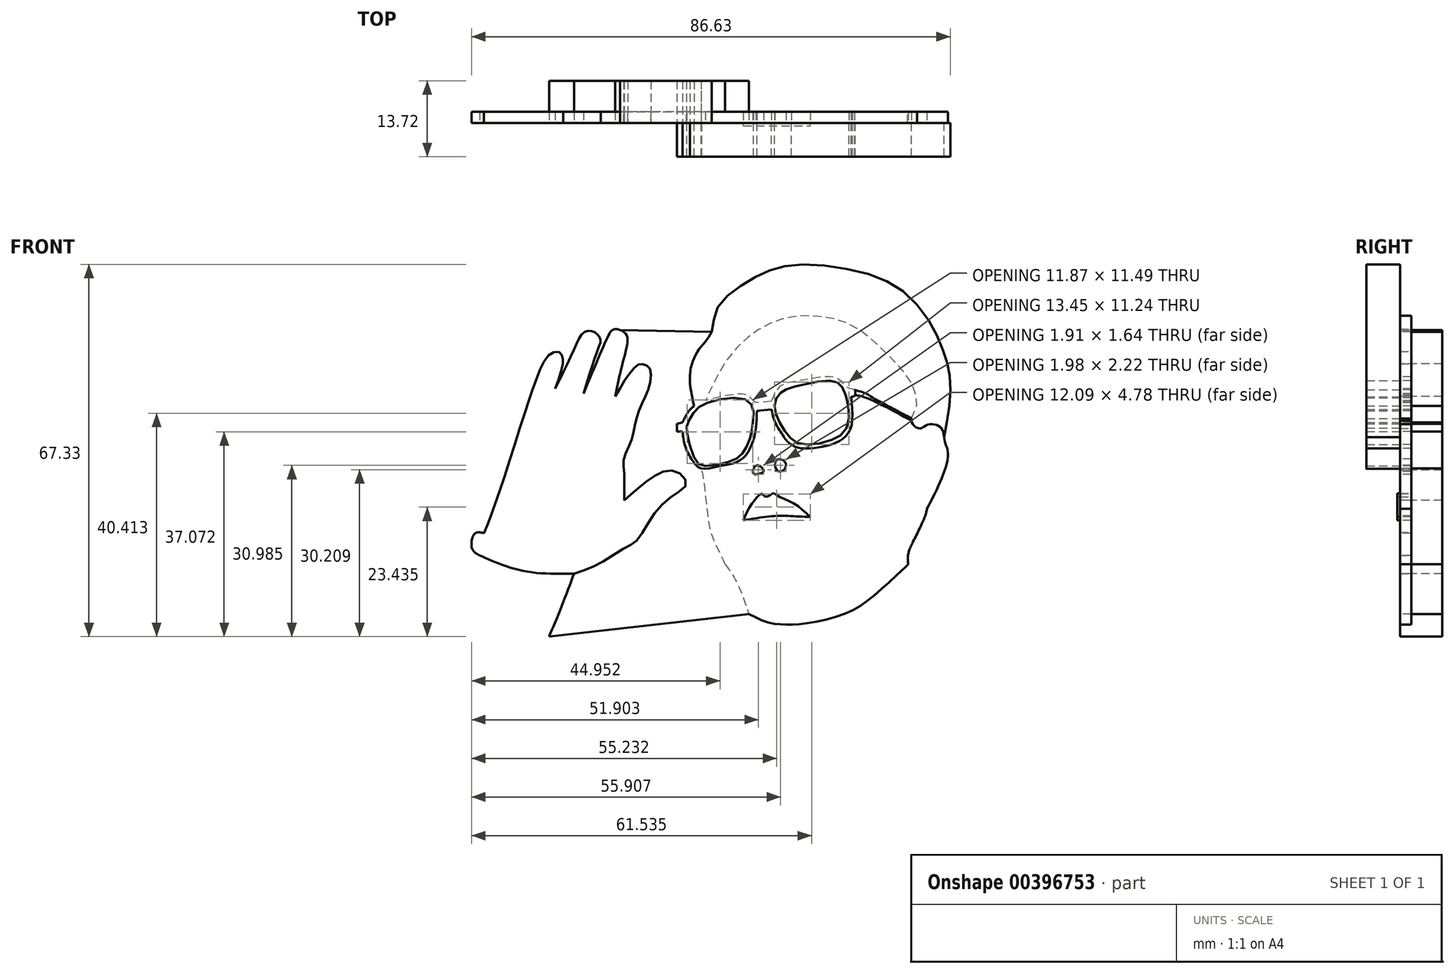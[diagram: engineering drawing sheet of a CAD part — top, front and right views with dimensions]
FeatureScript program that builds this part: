
annotation { "Feature Type Name" : "Feature", "Feature Type Description" : "" }
export const myFeature = defineFeature(function(context is Context, id is Id, definition is map)
    precondition{}
    {
        {
            var Q0;
            Q0=qCreatedBy(makeId("Front.planeOp"),FACE);
            var sketch = newSketch(context, id + "F0", { "sketchPlane" : qUnion([Q0])});
            skFitSpline(sketch, "E0", {"points": [v(-10.9, 0) * mm, v(-12.43, 3.33) * mm, v(-13.41, 5.64) * mm, v(-14.1, 9.87) * mm, v(-15.17, 17.33) * mm, v(-15.24, 17.33) * mm], "startDerivative": vector(-7.08, 15.66) * mm, "endDerivative": vector(-2.12, -1.22) * mm});
            skFitSpline(sketch, "E1", {"points": [v(-5.76, 16.4) * mm, v(-4.7, 16.4) * mm, v(-3.91, 16.94) * mm, v(-4.74, 17.86) * mm, v(-5.18, 17.9) * mm, v(-5.71, 17.47) * mm, v(-5.76, 16.4) * mm]});
            skFitSpline(sketch, "E2", {"points": [v(-1.54, 16.98) * mm, v(-0.66, 16.84) * mm, v(0, 17.52) * mm, v(0, 18.44) * mm, v(-1.05, 19.02) * mm, v(-1.78, 18.73) * mm, v(-1.54, 16.98) * mm]});
            skFitSpline(sketch, "E3", {"points": [v(-7.6, 7.95) * mm, v(-6.4, 10.53) * mm, v(-4.93, 12.32) * mm, v(-4.2, 12.76) * mm, v(-3.72, 12.27) * mm, v(-2.85, 12.47) * mm, v(-2.26, 12.86) * mm, v(-1.24, 12.32) * mm, v(1.67, 10.91) * mm, v(4.49, 8.56) * mm], "startDerivative": vector(7.43, 18.33) * mm, "endDerivative": vector(15.87, -15.6) * mm});
            skFitSpline(sketch, "E4", {"points": [v(-7.6, 7.95) * mm, v(-3.82, 8.56) * mm, v(-0.98, 8.77) * mm, v(1.7, 8.7) * mm, v(4.49, 8.56) * mm], "startDerivative": vector(13.93, 2.45) * mm, "endDerivative": vector(11.63, -0.59) * mm});
            skFitSpline(sketch, "E5", {"points": [v(-7.6, 7.95) * mm, v(-5.68, 9.87) * mm, v(-4.23, 9.87) * mm, v(-1.91, 10.5) * mm, v(1.29, 9.87) * mm, v(4.49, 8.56) * mm], "startDerivative": vector(9.45, 12.57) * mm, "endDerivative": vector(13.65, -5.86) * mm});
            skFitSpline(sketch, "E6", {"points": [v(0.58, 16.24) * mm, v(2.34, 17.42) * mm, v(2.4, 20.12) * mm, v(1.29, 21.11) * mm, v(1.11, 21.64) * mm], "startDerivative": vector(7.2, 2.7) * mm, "endDerivative": vector(-0.35, 3.73) * mm});
            skFitSpline(sketch, "E7", {"points": [v(-5.7, 15.07) * mm, v(-7.05, 16.18) * mm, v(-7.22, 18.18) * mm, v(-5.82, 19.82) * mm], "startDerivative": vector(-4.98, 2.85) * mm, "endDerivative": vector(5, 4.2) * mm});
            skFitSpline(sketch, "E8", {"points": [v(-10.9, 0) * mm, v(-8.85, -3.14) * mm, v(-6.61, -8.97) * mm], "startDerivative": vector(4.87, -6.5) * mm, "endDerivative": vector(3.76, -11.24) * mm});
            skFitSpline(sketch, "E9", {"points": [v(-6.61, -8.97) * mm, v(-2.94, -10.56) * mm, v(0, -10.88) * mm, v(3.45, -10.72) * mm, v(10.71, -8.97) * mm, v(15.74, -5.85) * mm, v(20.85, -1.3) * mm, v(22.22, 0) * mm], "startDerivative": vector(27.5, -14.14) * mm, "endDerivative": vector(11.85, 11.52) * mm});
            skFitSpline(sketch, "E10", {"points": [v(22.22, 0) * mm, v(22.22, 1.86) * mm, v(23.68, 5.27) * mm, v(25.22, 8.6) * mm, v(25.62, 10.05) * mm], "startDerivative": vector(-1.02, 8.24) * mm, "endDerivative": vector(1.53, 6.93) * mm});
            skFitSpline(sketch, "E11", {"points": [v(23.07, 4.07) * mm, v(22.95, 5.27) * mm, v(23.68, 9.65) * mm], "startDerivative": vector(-0.65, 2.97) * mm, "endDerivative": vector(1.6, 7.7) * mm});
            skFitSpline(sketch, "E12", {"points": [v(25.62, 10.05) * mm, v(27.81, 14.51) * mm, v(29.44, 19.95) * mm, v(28.87, 22.14) * mm, v(28.54, 23.92) * mm, v(27.73, 25.06) * mm, v(25.62, 25.22) * mm, v(24.32, 24.57) * mm, v(22.95, 25.55) * mm, v(22.95, 26.93) * mm, v(23.68, 28.3) * mm, v(22.95, 32.52) * mm, v(18.08, 38.36) * mm, v(11.91, 43.31) * mm, v(4.86, 44.93) * mm, v(0, 44.53) * mm, v(-5.2, 42.26) * mm, v(-10.56, 36.98) * mm, v(-14.45, 29.6) * mm], "startDerivative": vector(34.38, 66.1) * mm, "endDerivative": vector(-42.74, -94.88) * mm});
            skFitSpline(sketch, "E13", {"points": [v(28.7, 23.02) * mm, v(29.66, 28.67) * mm, v(29.74, 33.99) * mm, v(28.87, 37.67) * mm, v(26.63, 42.99) * mm, v(21.23, 49.45) * mm, v(12.96, 53.05) * mm, v(2, 54.2) * mm, v(-3.9, 52.73) * mm, v(-9.27, 49.54) * mm, v(-12.68, 45.63) * mm, v(-13.35, 42.05) * mm, v(-15.5, 39.05) * mm, v(-17.26, 34.47) * mm, v(-16.5, 28.64) * mm], "startDerivative": vector(15.76, 79.49) * mm, "endDerivative": vector(19.32, -83.28) * mm});
            skFitSpline(sketch, "E14", {"points": [v(1.36, 26.58) * mm, v(4.9, 26.99) * mm, v(8.36, 27.56) * mm, v(5.48, 28.22) * mm, v(4.08, 28.47) * mm, v(1.36, 26.58) * mm]});
            skFitSpline(sketch, "E15", {"points": [v(3.3, 28.12) * mm, v(3.32, 27.5) * mm, v(3.66, 26.76) * mm], "startDerivative": vector(-0.1, -1.32) * mm, "endDerivative": vector(0.8, -1.48) * mm});
            skFitSpline(sketch, "E16", {"points": [v(5.48, 28.22) * mm, v(5.48, 27.64) * mm, v(5.2, 27.04) * mm], "startDerivative": vector(0.12, -1.23) * mm, "endDerivative": vector(-0.62, -1.28) * mm});
            skFitSpline(sketch, "E17", {"points": [v(-11.5, 23.7) * mm, v(-10.57, 24.74) * mm, v(-10.06, 25.18) * mm, v(-9.09, 25.38) * mm, v(-7.27, 25.28) * mm, v(-6.77, 24.88) * mm, v(-6.8, 24.85) * mm], "startDerivative": vector(4.66, 5.17) * mm, "endDerivative": vector(-1.21, -0.56) * mm});
            skFitSpline(sketch, "E18", {"points": [v(-11.5, 23.7) * mm, v(-9.7, 23.7) * mm, v(-6.77, 24.88) * mm], "startDerivative": vector(4, -0.45) * mm, "endDerivative": vector(5.41, 2.66) * mm});
            skFitSpline(sketch, "E19", {"points": [v(-10.57, 24.74) * mm, v(-10.3, 24.14) * mm, v(-9.7, 23.7) * mm], "startDerivative": vector(0.4, -1.34) * mm, "endDerivative": vector(1.34, -0.75) * mm});
            skFitSpline(sketch, "E20", {"points": [v(-8.14, 25.43) * mm, v(-8.18, 24.88) * mm, v(-8.3, 24.16) * mm], "startDerivative": vector(-0.04, -1.14) * mm, "endDerivative": vector(-0.27, -1.36) * mm});
            skFitSpline(sketch, "E21", {"points": [v(-5.15, 27.77) * mm, v(-2.53, 28) * mm], "startDerivative": vector(2.63, 0.24) * mm, "endDerivative": vector(2.63, 0.24) * mm});
            skFitSpline(sketch, "E22", {"points": [v(-2.53, 28) * mm, v(-1.8, 25.52) * mm, v(-0.7, 23.7) * mm, v(0.33, 22.25) * mm, v(1.11, 21.64) * mm], "startDerivative": vector(2.04, -8.75) * mm, "endDerivative": vector(4.25, -2.72) * mm});
            skFitSpline(sketch, "E23", {"points": [v(1.11, 21.64) * mm, v(2.22, 21.1) * mm, v(5.48, 21.07) * mm, v(9.27, 22.07) * mm, v(11.72, 24.38) * mm, v(11.89, 30.28) * mm], "startDerivative": vector(7.71, -5.2) * mm, "endDerivative": vector(-2.5, 25.05) * mm});
            skFitSpline(sketch, "E24", {"points": [v(11.89, 30.28) * mm, v(12.54, 30.57) * mm, v(12.51, 31.6) * mm, v(11.52, 31.82) * mm, v(9.67, 33.47) * mm, v(6.2, 33.84) * mm, v(2.25, 33.15) * mm, v(-0.93, 32.24) * mm, v(-2.53, 29.46) * mm], "startDerivative": vector(10.84, 1.27) * mm, "endDerivative": vector(-8.07, -21.78) * mm});
            skFitSpline(sketch, "E25", {"points": [v(-2.53, 29.46) * mm, v(-5.35, 29.22) * mm], "startDerivative": vector(-2.82, -0.24) * mm, "endDerivative": vector(-2.82, -0.24) * mm});
            skFitSpline(sketch, "E26", {"points": [v(-5.35, 29.22) * mm, v(-6.5, 30.28) * mm, v(-8.09, 30.8) * mm, v(-14.45, 29.6) * mm, v(-16.5, 28.64) * mm, v(-17.58, 27.56) * mm, v(-18.6, 25.69) * mm], "startDerivative": vector(-8.55, 8.6) * mm, "endDerivative": vector(-6.15, -12.85) * mm});
            skFitSpline(sketch, "E27", {"points": [v(-18.6, 25.69) * mm, v(-19.64, 25.4) * mm], "startDerivative": vector(-1.04, -0.28) * mm, "endDerivative": vector(-1.04, -0.28) * mm});
            skFitSpline(sketch, "E28", {"points": [v(-19.64, 25.4) * mm, v(-19.64, 24) * mm], "startDerivative": vector(0, -1.41) * mm, "endDerivative": vector(0, -1.41) * mm});
            skFitSpline(sketch, "E29", {"points": [v(-19.64, 24) * mm, v(-18.6, 24) * mm], "startDerivative": vector(1.04, 0) * mm, "endDerivative": vector(1.04, 0) * mm});
            skFitSpline(sketch, "E30", {"points": [v(-18.6, 24) * mm, v(-18.34, 22.17) * mm, v(-17.72, 20.35) * mm, v(-16.74, 18.65) * mm, v(-16.21, 18.03) * mm, v(-15.17, 17.33) * mm, v(-12.14, 17.71) * mm, v(-9.7, 18.18) * mm, v(-7.63, 19.27) * mm, v(-6.09, 21.64) * mm, v(-5.35, 24.57) * mm, v(-5.15, 27.77) * mm], "startDerivative": vector(2.35, -22.1) * mm, "endDerivative": vector(0.85, 29.27) * mm});
            skFitSpline(sketch, "E31", {"points": [v(12.51, 31.6) * mm, v(14.65, 30.88) * mm, v(15.17, 30.53) * mm, v(22.8, 26.4) * mm], "startDerivative": vector(9.16, -2.74) * mm, "endDerivative": vector(17.9, -9.4) * mm});
            skFitSpline(sketch, "E32", {"points": [v(12.54, 30.57) * mm, v(14.2, 30.28) * mm, v(22.8, 25.99) * mm], "startDerivative": vector(4.64, -0.2) * mm, "endDerivative": vector(14.51, -7.9) * mm});
            skFitSpline(sketch, "E33", {"points": [v(-17.77, 23.7) * mm, v(-17.7, 25.4) * mm, v(-16.5, 27.56) * mm, v(-14.14, 29.22) * mm, v(-7.8, 30) * mm, v(-5.95, 28.47) * mm, v(-5.83, 26) * mm, v(-6.46, 22.56) * mm, v(-7.8, 20.05) * mm, v(-9.7, 18.72) * mm, v(-14.45, 17.82) * mm, v(-16.17, 18.65) * mm, v(-17.77, 23.7) * mm]});
            skFitSpline(sketch, "E34", {"points": [v(-38.24, -1.7) * mm, v(-33.9, 0) * mm, v(-28.9, 3.04) * mm, v(-26.86, 4.4) * mm, v(-24.01, 8.73) * mm, v(-20.22, 12.52) * mm, v(-17.92, 14.55) * mm, v(-19.55, 16.73) * mm, v(-22.53, 16.6) * mm, v(-26.32, 14.02) * mm, v(-29.17, 11.58) * mm], "startDerivative": vector(38.53, 12.33) * mm, "endDerivative": vector(-27.75, -24.31) * mm});
            skFitSpline(sketch, "E35", {"points": [v(-29.17, 11.58) * mm, v(-29.17, 16.4) * mm, v(-29.17, 19.28) * mm, v(-27.87, 22.41) * mm, v(-27.16, 25.48) * mm, v(-25.92, 29.12) * mm, v(-24.6, 32.3) * mm, v(-24.5, 35.32) * mm, v(-25.39, 36.11) * mm, v(-26.45, 36.2) * mm, v(-28.14, 34.6) * mm, v(-30.8, 30.36) * mm], "startDerivative": vector(1.17, 44.46) * mm, "endDerivative": vector(-22.87, -39.18) * mm});
            skFitSpline(sketch, "E36", {"points": [v(-30.8, 30.36) * mm, v(-29.9, 34.6) * mm, v(-28.78, 39.05) * mm, v(-28.68, 41.38) * mm, v(-29.9, 42.4) * mm, v(-31.2, 42.44) * mm, v(-32.12, 41.18) * mm, v(-36.53, 30.9) * mm], "startDerivative": vector(5.03, 25.38) * mm, "endDerivative": vector(-20.15, -47.92) * mm});
            skFitSpline(sketch, "E37", {"points": [v(-36.53, 30.9) * mm, v(-33.96, 38.8) * mm, v(-33.43, 40.7) * mm, v(-34.01, 41.62) * mm, v(-35.08, 42.2) * mm, v(-36.53, 41.91) * mm, v(-38.08, 39.2) * mm, v(-41.62, 31.78) * mm], "startDerivative": vector(12.04, 39.18) * mm, "endDerivative": vector(-17.06, -34.62) * mm});
            skFitSpline(sketch, "E38", {"points": [v(-41.62, 31.78) * mm, v(-40.3, 36.14) * mm, v(-40.3, 37.45) * mm, v(-40.85, 38.37) * mm, v(-42.45, 38.13) * mm, v(-44.48, 34.98) * mm, v(-47.24, 27.08) * mm, v(-52, 12.35) * mm, v(-54.51, 5.6) * mm], "startDerivative": vector(13.64, 39.93) * mm, "endDerivative": vector(-14.7, -37.19) * mm});
            skFitSpline(sketch, "E39", {"points": [v(-29.17, 16.4) * mm, v(-32.41, 17.1) * mm, v(-35.66, 17.39) * mm, v(-41.62, 16.4) * mm], "startDerivative": vector(-11.03, 2.47) * mm, "endDerivative": vector(-15.91, -3.37) * mm});
            skFitSpline(sketch, "E40", {"points": [v(-34.05, 17.34) * mm, v(-34.79, 16.4) * mm, v(-36.53, 14.24) * mm, v(-38.13, 13.07) * mm, v(-39.78, 10.4) * mm, v(-39.73, 10.36) * mm], "startDerivative": vector(-3.73, -4.24) * mm, "endDerivative": vector(1.63, -0.43) * mm});
            skFitSpline(sketch, "E41", {"points": [v(-45.95, 21.15) * mm, v(-40.3, 19.33) * mm, v(-36.53, 20.15) * mm], "startDerivative": vector(10.7, -4.71) * mm, "endDerivative": vector(8.04, 3) * mm});
            skFitSpline(sketch, "E42", {"points": [v(-54.51, 5.6) * mm, v(-56.14, 5.6) * mm, v(-56.68, 2.89) * mm, v(-54.51, 1.27) * mm, v(-47.83, -1.1) * mm, v(-38.24, -1.7) * mm], "startDerivative": vector(-14.56, 4.39) * mm, "endDerivative": vector(32.95, 0.31) * mm});
            skFitSpline(sketch, "E43", {"points": [v(-38.24, -1.7) * mm, v(-40.81, -8.44) * mm, v(-42.75, -13.09) * mm], "startDerivative": vector(-4.85, -12.96) * mm, "endDerivative": vector(-4.17, -9.7) * mm});
            skFitSpline(sketch, "E44", {"points": [v(-42.75, -13.09) * mm, v(-47.72, -13.09) * mm, v(-56.78, -11.47) * mm, v(-58.62, -10.39) * mm], "startDerivative": vector(-12.86, -0.73) * mm, "endDerivative": vector(-6.1, 5.04) * mm});
            skFitSpline(sketch, "E45", {"points": [v(-58.62, -10.39) * mm, v(-55.92, -7.04) * mm, v(-55.12, -1.7) * mm, v(-55.32, 1.62) * mm, v(-55.27, 1.6) * mm], "startDerivative": vector(9.66, 9.46) * mm, "endDerivative": vector(1.4, -1.31) * mm});
            skFitSpline(sketch, "E46", {"points": [v(-58.62, -10.39) * mm, v(-59.32, -11.02) * mm, v(-60.87, -7.73) * mm], "startDerivative": vector(-2.04, -3.05) * mm, "endDerivative": vector(-2.41, 7.26) * mm});
            skFitSpline(sketch, "E47", {"points": [v(-60.87, -7.73) * mm, v(-56.68, 2.89) * mm], "startDerivative": vector(4.2, 10.61) * mm, "endDerivative": vector(4.2, 10.61) * mm});
            skFitSpline(sketch, "E48", {"points": [v(-42.75, -13.09) * mm, v(-6.61, -8.97) * mm], "startDerivative": vector(36.14, 4.12) * mm, "endDerivative": vector(36.14, 4.12) * mm});
            skFitSpline(sketch, "E49", {"points": [v(-29.9, 42.4) * mm, v(-13.35, 42.05) * mm], "startDerivative": vector(16.55, -0.35) * mm, "endDerivative": vector(16.55, -0.35) * mm});
            skFitSpline(sketch, "E50", {"points": [v(-1.98, 28.73) * mm, v(-1.14, 25.9) * mm, v(0.67, 23.1) * mm, v(2.9, 21.76) * mm, v(8.34, 22.5) * mm, v(11.08, 24.69) * mm, v(11.27, 29.29) * mm, v(10.13, 32.25) * mm, v(8.43, 33.21) * mm, v(3.27, 32.52) * mm, v(0, 31.6) * mm, v(-1.3, 30.51) * mm, v(-1.98, 28.73) * mm]});
            skSolve(sketch);
        }
        {
            var Q0;
            {var subQ1=sQuery(id+"F0.wireOp",EDGE,"E34");Q0=makeQuery(id+"F0.imprint","IMPRINT",FACE,{"disambiguationData":[TD([[makeQuery(id+"F0.imprint","IMPRINT",EDGE,{"derivedFrom":subQ1}),1.0]])]});}
            var Q1;
            Q1=makeQuery(id+"F0.imprint","IMPRINT",FACE,{"disambiguationData":[TD([[makeQuery(id+"F0.imprint","IMPRINT",EDGE,{"derivedFrom":sQuery(id+"F0.wireOp",EDGE,"E1")}),-1.0]])]});
            var Q2;
            {var subQ3=sQuery(id+"F0.wireOp",EDGE,"E25");Q2=makeQuery(id+"F0.imprint","IMPRINT",FACE,{"disambiguationData":[TD([[makeQuery(id+"F0.imprint","IMPRINT",EDGE,{"derivedFrom":subQ3}),-1.0]])]});}
            var Q3;
            {var subQ0=sQuery(id+"F0.wireOp",EDGE,"E15");Q3=makeQuery(id+"F0.imprint","IMPRINT",FACE,{"disambiguationData":[TD([[makeQuery(id+"F0.imprint","IMPRINT",EDGE,{"derivedFrom":subQ0}),-1.0]])]});}
            var Q4;
            {var subQ0=sQuery(id+"F0.wireOp",EDGE,"E16");Q4=makeQuery(id+"F0.imprint","IMPRINT",FACE,{"disambiguationData":[TD([[makeQuery(id+"F0.imprint","IMPRINT",EDGE,{"derivedFrom":subQ0}),1.0]])]});}
            var Q5;
            {var subQ0=sQuery(id+"F0.wireOp",EDGE,"E19");Q5=makeQuery(id+"F0.imprint","IMPRINT",FACE,{"disambiguationData":[TD([[makeQuery(id+"F0.imprint","IMPRINT",EDGE,{"derivedFrom":subQ0}),1.0]])]});}
            var Q6;
            {var subQ3=sQuery(id+"F0.wireOp",EDGE,"E20");Q6=makeQuery(id+"F0.imprint","IMPRINT",FACE,{"disambiguationData":[TD([[makeQuery(id+"F0.imprint","IMPRINT",EDGE,{"derivedFrom":subQ3}),1.0]])]});}
            var Q7;
            {var subQ3=sQuery(id+"F0.wireOp",EDGE,"E19");Q7=makeQuery(id+"F0.imprint","IMPRINT",FACE,{"disambiguationData":[TD([[makeQuery(id+"F0.imprint","IMPRINT",EDGE,{"derivedFrom":subQ3}),-1.0]])]});}
            var Q8;
            {var subQ0=sQuery(id+"F0.wireOp",EDGE,"E15");Q8=makeQuery(id+"F0.imprint","IMPRINT",FACE,{"disambiguationData":[TD([[makeQuery(id+"F0.imprint","IMPRINT",EDGE,{"derivedFrom":subQ0}),1.0]])]});}
            var Q9;
            Q9=makeQuery(id+"F0.imprint","IMPRINT",FACE,{"disambiguationData":[TD([[makeQuery(id+"F0.imprint","IMPRINT",EDGE,{"derivedFrom":sQuery(id+"F0.wireOp",EDGE,"E33")}),-1.0]])]});
            var Q10;
            Q10=makeQuery(id+"F0.imprint","IMPRINT",FACE,{"disambiguationData":[TD([[makeQuery(id+"F0.imprint","IMPRINT",EDGE,{"derivedFrom":sQuery(id+"F0.wireOp",EDGE,"E50")}),1.0]])]});
            extrude(context, id + "F1", {"entities" : qUnion([Q0, Q1, Q2, Q3, Q4, Q5, Q6, Q7, Q8, Q9, Q10]), "oppositeDirection" : true, "depth" : 2.03 * mm});
        }
        {
            var Q0;
            {var subQ8=sQuery(id+"F0.wireOp",EDGE,"E8");Q0=makeQuery(id+"F0.imprint","IMPRINT",FACE,{"disambiguationData":[TD([[makeQuery(id+"F0.imprint","IMPRINT",EDGE,{"derivedFrom":subQ8}),-1.0]])]});}
            extrude(context, id + "F2", {"entities" : qUnion([Q0]), "oppositeDirection" : true, "depth" : 7.62 * mm});
        }
        {
            var Q0;
            {var subQ12=sQuery(id+"F0.wireOp",EDGE,"E21");Q0=makeQuery(id+"F0.imprint","IMPRINT",FACE,{"disambiguationData":[TD([[makeQuery(id+"F0.imprint","IMPRINT",EDGE,{"derivedFrom":subQ12}),1.0]])]});}
            var Q1;
            {var subQ3=sQuery(id+"F0.wireOp",EDGE,"E25");Q1=makeQuery(id+"F0.imprint","IMPRINT",FACE,{"disambiguationData":[TD([[makeQuery(id+"F0.imprint","IMPRINT",EDGE,{"derivedFrom":subQ3}),-1.0]])]});}
            var Q2;
            {var subQ0=sQuery(id+"F0.wireOp",EDGE,"E13");var subQ1=sQuery(id+"F0.wireOp",EDGE,"E12");var subQ2=makeQuery(id+"F0.imprint","INTERSECT",VERTEX,{"derivedFrom":[subQ1,subQ0]});Q2=makeQuery(id+"F0.imprint","IMPRINT",FACE,{"disambiguationData":[TD([[makeQuery(id+"F0.imprint","IMPRINT",EDGE,{"disambiguationData":[TD([[subQ2,-1.0]])],"derivedFrom":subQ1}),-1.0]])]});}
            extrude(context, id + "F3", {"entities" : qUnion([Q0, Q1, Q2]), "operationType" : NewBodyOperationType.ADD, "depth" : 6.1 * mm});
        }
        {
            var Q0;
            Q0=makeQuery(id+"F0.imprint","IMPRINT",FACE,{"disambiguationData":[TD([[makeQuery(id+"F0.imprint","IMPRINT",EDGE,{"derivedFrom":sQuery(id+"F0.wireOp",EDGE,"E3")}),-1.0]])]});
            var Q1;
            Q1=makeQuery(id+"F0.imprint","IMPRINT",FACE,{"disambiguationData":[TD([[makeQuery(id+"F0.imprint","IMPRINT",EDGE,{"derivedFrom":sQuery(id+"F0.wireOp",EDGE,"E4")}),1.0]])]});
            extrude(context, id + "F4", {"entities" : qUnion([Q0, Q1]), "depth" : 0.5 * mm});
        }
    });
